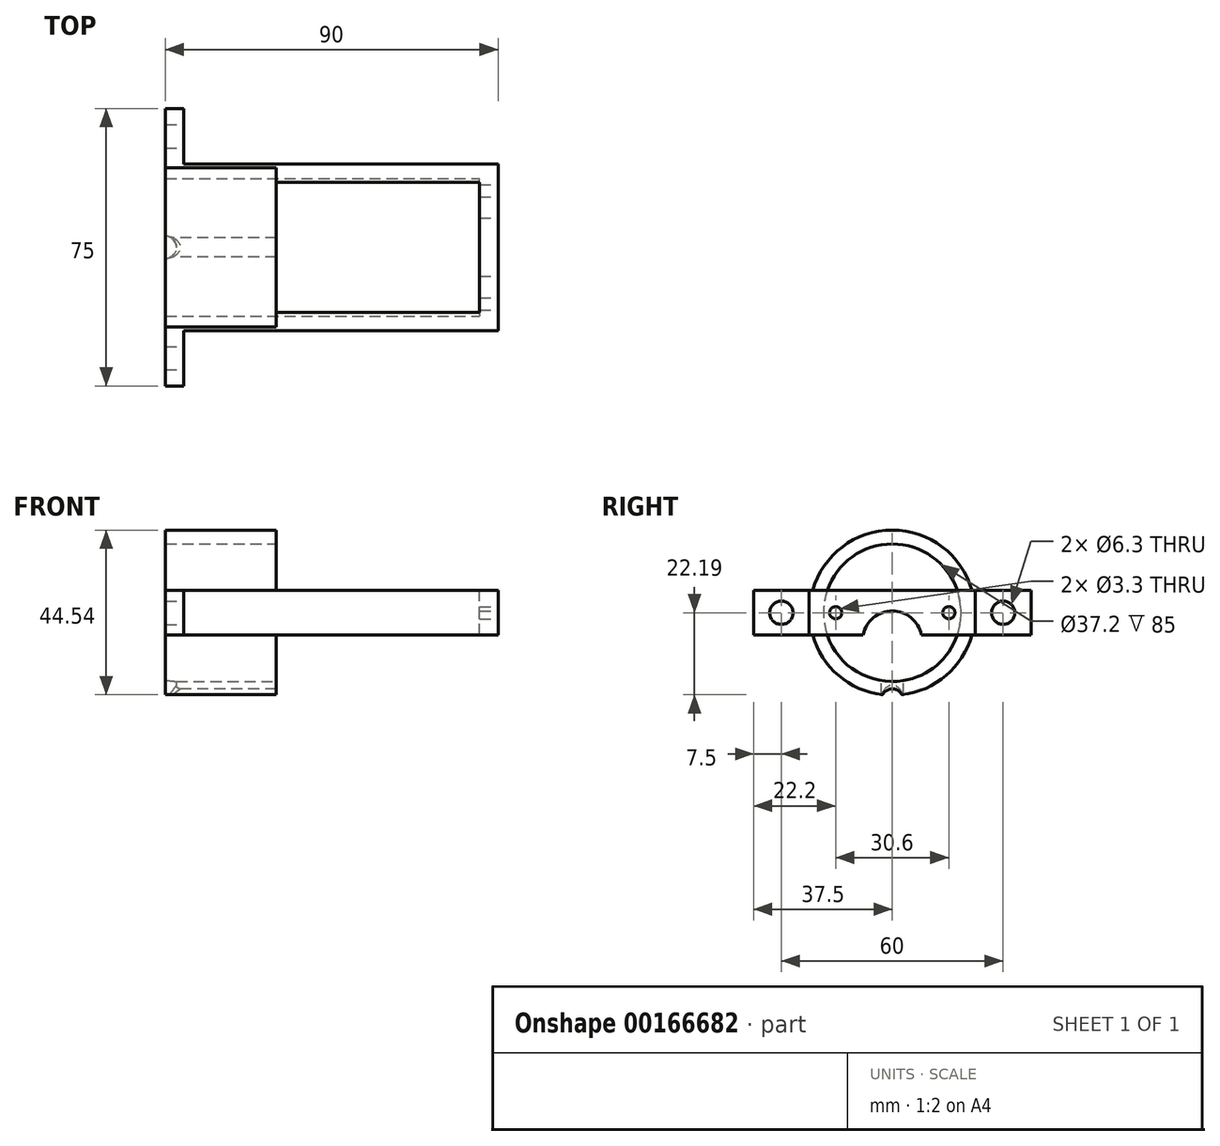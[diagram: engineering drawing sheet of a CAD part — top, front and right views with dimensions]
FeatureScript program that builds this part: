
annotation { "Feature Type Name" : "Feature", "Feature Type Description" : "" }
export const myFeature = defineFeature(function(context is Context, id is Id, definition is map)
    precondition{}
    {
        {
            var Q0;
            Q0=qCreatedBy(makeId("Top.planeOp"),FACE);
            var sketch = newSketch(context, id + "F0", { "sketchPlane" : qUnion([Q0])});
            skLineSegment(sketch, "E0", {"start": v(90, 0) * mm, "end": v(90, -22.5) * mm});
            skLineSegment(sketch, "E1", {"start": v(90, -22.5) * mm, "end": v(5, -22.5) * mm});
            skLineSegment(sketch, "E2", {"start": v(5, -22.5) * mm, "end": v(5, -37.5) * mm});
            skLineSegment(sketch, "E3", {"start": v(5, -37.5) * mm, "end": v(0, -37.5) * mm});
            skLineSegment(sketch, "E4", {"start": v(0, -37.5) * mm, "end": v(0, -17.5) * mm});
            skLineSegment(sketch, "E5", {"start": v(0, -17.5) * mm, "end": v(85, -17.5) * mm});
            skLineSegment(sketch, "E6", {"start": v(85, -17.5) * mm, "end": v(85, 0) * mm});
            skLineSegment(sketch, "E7.MirrorCS", {"start": v(5, 37.5) * mm, "end": v(0, 37.5) * mm});
            skLineSegment(sketch, "E8.MirrorCS", {"start": v(85, 17.5) * mm, "end": v(85, 0) * mm});
            skLineSegment(sketch, "E9.MirrorCS", {"start": v(0, 17.5) * mm, "end": v(85, 17.5) * mm});
            skLineSegment(sketch, "E10.MirrorCS", {"start": v(0, 37.5) * mm, "end": v(0, 17.5) * mm});
            skLineSegment(sketch, "E11.MirrorCS", {"start": v(5, 22.5) * mm, "end": v(5, 37.5) * mm});
            skLineSegment(sketch, "E12.MirrorCS", {"start": v(90, 0) * mm, "end": v(90, 22.5) * mm});
            skLineSegment(sketch, "E13.MirrorCS", {"start": v(90, 22.5) * mm, "end": v(5, 22.5) * mm});
            skLineSegment(sketch, "E14", {"start": v(-47.63, -18.6) * mm, "end": v(121.52, -18.6) * mm, "construction": true});
            skSolve(sketch);
        }
        {
            var Q0;
            Q0 = qSketchRegion(id + "F0", true);
            extrude(context, id + "F1", {"entities" : qUnion([Q0]), "depth" : 12 * mm, "symmetric" : true});
        }
        {
            var Q0;
            Q0=makeQuery(id+"F1.opExtrude","SWEPT_FACE",FACE,{"disambiguationData":[OSD([sQuery(id+"F0.wireOp",EDGE,"E0"),sQuery(id+"F0.wireOp",EDGE,"E12.MirrorCS")])]});
            var sketch = newSketch(context, id + "F2", { "sketchPlane" : qUnion([Q0])});
            skCircle(sketch, "E15", {"center": v(-15.3, 0) * mm, "radius": 1.65 * mm});
            skCircle(sketch, "E16", {"center": v(15.3, 0) * mm, "radius": 1.65 * mm});
            skCircle(sketch, "E17", {"center": v(0, -7.5) * mm, "radius": 8 * mm});
            skCircle(sketch, "E18", {"center": v(-30, 0) * mm, "radius": 3.15 * mm});
            skCircle(sketch, "E19", {"center": v(30, 0) * mm, "radius": 3.15 * mm});
            skSolve(sketch);
        }
        {
            var Q0;
            Q0 = qSketchRegion(id + "F2", true);
            extrude(context, id + "F3", {"entities" : qUnion([Q0]), "operationType" : NewBodyOperationType.REMOVE, "endBound" : BoundingType.THROUGH_ALL, "oppositeDirection" : true, "depth" : 25 * mm});
        }
        {
            var Q0;
            Q0=makeQuery(id+"F1.opExtrude","SWEPT_FACE",FACE,{"disambiguationData":[OSD([sQuery(id+"F0.wireOp",EDGE,"E6"),sQuery(id+"F0.wireOp",EDGE,"E8.MirrorCS")])]});
            var sketch = newSketch(context, id + "F4", { "sketchPlane" : qUnion([Q0])});
            skCircle(sketch, "E20", {"center": v(0, 0) * mm, "radius": 18.6 * mm});
            skSolve(sketch);
        }
        {
            var Q0;
            Q0 = qSketchRegion(id + "F4", true);
            extrude(context, id + "F5", {"entities" : qUnion([Q0]), "operationType" : NewBodyOperationType.REMOVE, "endBound" : BoundingType.THROUGH_ALL, "depth" : 25 * mm});
        }
        {
            var Q0;
            Q0=qCreatedBy(makeId("Right.planeOp"),FACE);
            var sketch = newSketch(context, id + "F6", { "sketchPlane" : qUnion([Q0])});
            skCircle(sketch, "E21", {"center": v(0, 0) * mm, "radius": 18.6 * mm});
            skCircle(sketch, "E22", {"center": v(0, 0) * mm, "radius": 22.35 * mm});
            skSolve(sketch);
        }
        {
            var Q0;
            Q0 = qSketchRegion(id + "F6", true);
            extrude(context, id + "F7", {"entities" : qUnion([Q0]), "operationType" : NewBodyOperationType.ADD, "depth" : 30 * mm});
        }
        {
            var Q0;
            Q0=qCreatedBy(makeId("Right.planeOp"),FACE);
            var sketch = newSketch(context, id + "F8", { "sketchPlane" : qUnion([Q0])});
            skCircle(sketch, "E23", {"center": v(0, -23.6) * mm, "radius": 3 * mm});
            skSolve(sketch);
        }
        {
            var Q0;
            Q0 = qSketchRegion(id + "F8", true);
            extrude(context, id + "F9", {"entities" : qUnion([Q0]), "operationType" : NewBodyOperationType.REMOVE, "endBound" : BoundingType.THROUGH_ALL, "depth" : 25 * mm});
        }
        {
            var Q0;
            Q0=qCreatedBy(makeId("Top.planeOp"),FACE);
            var sketch = newSketch(context, id + "F10", { "sketchPlane" : qUnion([Q0])});
            skCircle(sketch, "E24", {"center": v(0, 0) * mm, "radius": 3 * mm});
            skSolve(sketch);
        }
        {
            var Q0;
            Q0 = qSketchRegion(id + "F10", true);
            extrude(context, id + "F11", {"entities" : qUnion([Q0]), "operationType" : NewBodyOperationType.REMOVE, "endBound" : BoundingType.THROUGH_ALL, "oppositeDirection" : true, "depth" : 25 * mm});
        }
        {
            var Q0;
            Q0=makeQuery(id+"F11.boolean.opBoolean","INTERSECT",EDGE,{"derivedFrom":[makeQuery(id+"F9.boolean.opBoolean","COPY",FACE,{"derivedFrom":makeQuery(id+"F9.opExtrude","SWEPT_FACE",FACE,{"disambiguationData":[OSD([sQuery(id+"F8.wireOp",EDGE,"E23")])]})}),makeQuery(id+"F11.opExtrude","SWEPT_FACE",FACE,{"disambiguationData":[OSD([sQuery(id+"F10.wireOp",EDGE,"E24")])]})]});
            fillet(context, id + "F12", {"entities" : qUnion([Q0]), "radius" : 1 * mm, "tangentPropagation" : true, "allowEdgeOverflow" : false});
        }
    });
